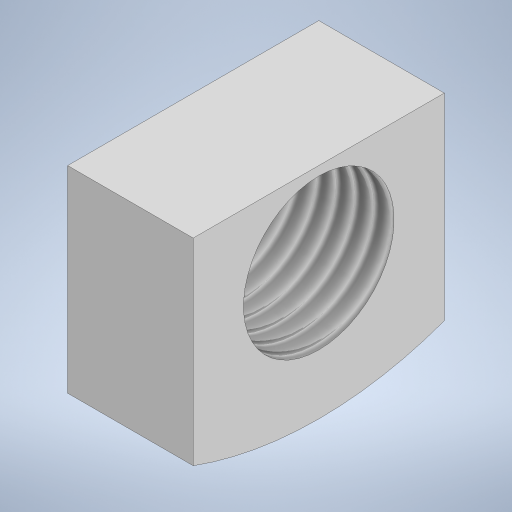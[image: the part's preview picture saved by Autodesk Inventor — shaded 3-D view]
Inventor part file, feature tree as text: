
AUTODESK INVENTOR PART (.ipt)
format: ipt  version: 2024 (Build 280153000, 153)  size: 211,456 bytes
history: native  units: mm
features: extrude x1, thread x1, sketch x1
ambient origin geometry x8: Origin, YZ Plane, XZ Plane, XY Plane, X Axis, Y Axis, Z Axis, Center Point
bodies: Solido1 (feature_tree)
feature tree (3):
  extrude  "Estrusione1"  Depth=10.0mm
  thread  "Filettatura1"
  sketch  "Schizzo1"
